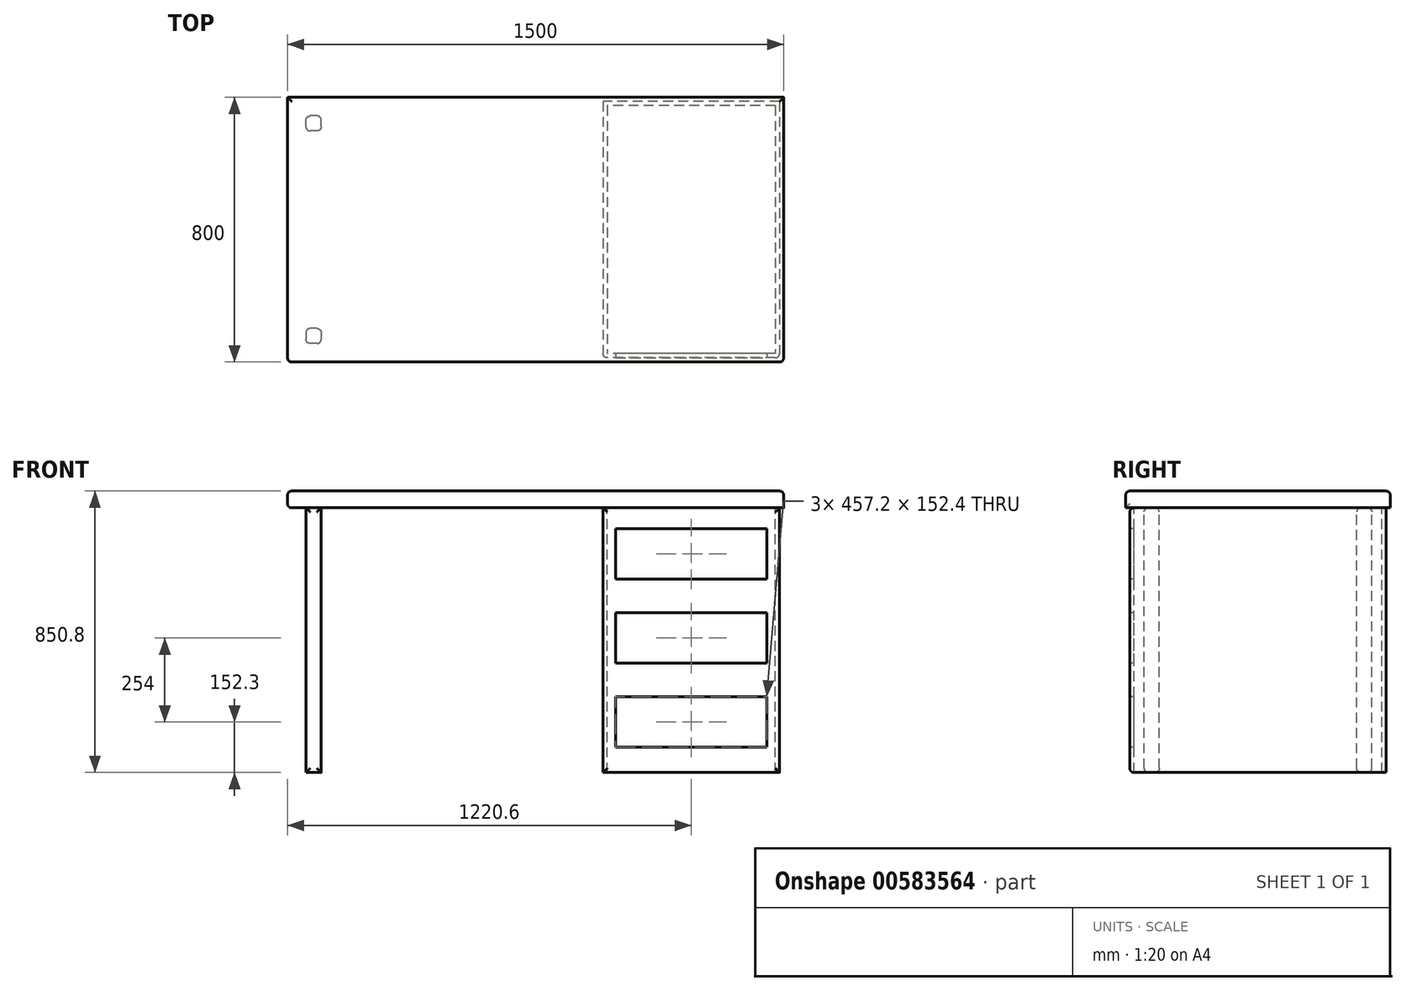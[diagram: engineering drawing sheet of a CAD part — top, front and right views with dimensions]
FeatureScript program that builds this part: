
annotation { "Feature Type Name" : "Feature", "Feature Type Description" : "" }
export const myFeature = defineFeature(function(context is Context, id is Id, definition is map)
    precondition{}
    {
        {
            var Q0;
            Q0=qCreatedBy(makeId("Top.planeOp"),FACE);
            var sketch = newSketch(context, id + "F0", { "sketchPlane" : qUnion([Q0])});
            skLineSegment(sketch, "E0.bottom", {"start": v(-750, 400) * mm, "end": v(750, 400) * mm});
            skLineSegment(sketch, "E0.top", {"start": v(-750, -400) * mm, "end": v(750, -400) * mm});
            skLineSegment(sketch, "E0.left", {"start": v(-750, 400) * mm, "end": v(-750, -400) * mm});
            skLineSegment(sketch, "E0.right", {"start": v(750, 400) * mm, "end": v(750, -400) * mm});
            skPoint(sketch, "E0.middle", {"position": v(0, 0) * mm});
            skSolve(sketch);
        }
        {
            var Q0;
            Q0 = qSketchRegion(id + "F0", true);
            extrude(context, id + "F1", {"entities" : qUnion([Q0]), "depth" : 50.8 * mm, "offsetDistance" : 25.4 * mm});
        }
        {
            var Q0;
            Q0=makeQuery(id+"F1.opExtrude","CAP_FACE",FACE,{"disambiguationData":[OSD([sQuery(id+"F0.wireOp",EDGE,"E0.bottom"),sQuery(id+"F0.wireOp",EDGE,"E0.top"),sQuery(id+"F0.wireOp",EDGE,"E0.left"),sQuery(id+"F0.wireOp",EDGE,"E0.right")])],"isStart":true});
            var sketch = newSketch(context, id + "F2", { "sketchPlane" : qUnion([Q0])});
            skLineSegment(sketch, "E1.bottom", {"start": v(-648.4, 298.4) * mm, "end": v(-694.12, 298.4) * mm});
            skLineSegment(sketch, "E1.top", {"start": v(-648.4, 344.12) * mm, "end": v(-694.12, 344.12) * mm});
            skLineSegment(sketch, "E1.left", {"start": v(-648.4, 298.4) * mm, "end": v(-648.4, 344.12) * mm});
            skLineSegment(sketch, "E1.right", {"start": v(-694.12, 298.4) * mm, "end": v(-694.12, 344.12) * mm});
            skPoint(sketch, "E1.middle", {"position": v(-671.26, 321.26) * mm});
            skLineSegment(sketch, "E2", {"start": v(0, 0) * mm, "end": v(-399.1, 0) * mm, "construction": true});
            skPoint(sketch, "E3.MirrorP", {"position": v(-671.26, -321.26) * mm});
            skLineSegment(sketch, "E4.MirrorCS", {"start": v(-648.4, -298.4) * mm, "end": v(-694.12, -298.4) * mm});
            skLineSegment(sketch, "E5.MirrorCS", {"start": v(-648.4, -344.12) * mm, "end": v(-694.12, -344.12) * mm});
            skLineSegment(sketch, "E6.MirrorCS", {"start": v(-648.4, -298.4) * mm, "end": v(-648.4, -344.12) * mm});
            skLineSegment(sketch, "E7.MirrorCS", {"start": v(-694.12, -298.4) * mm, "end": v(-694.12, -344.12) * mm});
            skSolve(sketch);
        }
        {
            var Q0;
            Q0=makeQuery(id+"F2.imprint","IMPRINT",FACE,{"disambiguationData":[TD([[makeQuery(id+"F2.imprint","IMPRINT",EDGE,{"derivedFrom":sQuery(id+"F2.wireOp",EDGE,"E1.bottom")}),-1.0]])]});
            var Q1;
            Q1=makeQuery(id+"F2.imprint","IMPRINT",FACE,{"disambiguationData":[TD([[makeQuery(id+"F2.imprint","IMPRINT",EDGE,{"derivedFrom":sQuery(id+"F2.wireOp",EDGE,"E4.MirrorCS")}),1.0]])]});
            extrude(context, id + "F3", {"entities" : qUnion([Q0, Q1]), "depth" : 800 * mm, "offsetDistance" : 25.4 * mm});
        }
        {
            var Q0;
            Q0=makeQuery(id+"F1.opExtrude","CAP_FACE",FACE,{"disambiguationData":[OSD([sQuery(id+"F0.wireOp",EDGE,"E0.bottom"),sQuery(id+"F0.wireOp",EDGE,"E0.top"),sQuery(id+"F0.wireOp",EDGE,"E0.left"),sQuery(id+"F0.wireOp",EDGE,"E0.right")])],"isStart":true});
            var sketch = newSketch(context, id + "F4", { "sketchPlane" : qUnion([Q0])});
            skLineSegment(sketch, "E8.bottom", {"start": v(724.6, -374.6) * mm, "end": v(216.6, -374.6) * mm});
            skLineSegment(sketch, "E8.top", {"start": v(724.6, 374.6) * mm, "end": v(216.6, 374.6) * mm});
            skLineSegment(sketch, "E8.left", {"start": v(724.6, -374.6) * mm, "end": v(724.6, 374.6) * mm});
            skLineSegment(sketch, "E8.right", {"start": v(216.6, -374.6) * mm, "end": v(216.6, 374.6) * mm});
            skPoint(sketch, "E8.middle", {"position": v(470.6, 0) * mm});
            skLineSegment(sketch, "E9.0", {"start": v(203.9, -387.3) * mm, "end": v(203.9, 387.3) * mm});
            skLineSegment(sketch, "E9.1", {"start": v(737.3, -387.3) * mm, "end": v(203.9, -387.3) * mm});
            skLineSegment(sketch, "E9.2", {"start": v(737.3, -387.3) * mm, "end": v(737.3, 387.3) * mm});
            skLineSegment(sketch, "E9.3", {"start": v(737.3, 387.3) * mm, "end": v(203.9, 387.3) * mm});
            skSolve(sketch);
        }
        {
            var Q0;
            Q0 = qSketchRegion(id + "F4", true);
            extrude(context, id + "F5", {"entities" : qUnion([Q0]), "depth" : 800 * mm, "offsetDistance" : 25.4 * mm});
        }
        {
            var Q0;
            Q0=makeQuery(id+"F5.opExtrude","SWEPT_FACE",FACE,{"disambiguationData":[OSD([sQuery(id+"F4.wireOp",EDGE,"E9.3")])]});
            var Q1;
            Q1=makeQuery(id+"F1.opExtrude","CAP_FACE",FACE,{"disambiguationData":[OSD([sQuery(id+"F0.wireOp",EDGE,"E0.bottom"),sQuery(id+"F0.wireOp",EDGE,"E0.top"),sQuery(id+"F0.wireOp",EDGE,"E0.left"),sQuery(id+"F0.wireOp",EDGE,"E0.right")])],"isStart":false});
            var Q2;
            Q2=makeQuery(id+"F1.opExtrude","CAP_EDGE",EDGE,{"disambiguationData":[OSD([sQuery(id+"F0.wireOp",EDGE,"E0.left")])],"isStart":true});
            var Q3;
            Q3=makeQuery(id+"F3.opExtrude","SWEPT_FACE",FACE,{"disambiguationData":[OSD([sQuery(id+"F2.wireOp",EDGE,"E1.top")])]});
            var Q4;
            Q4=makeQuery(id+"F3.opExtrude","SWEPT_FACE",FACE,{"disambiguationData":[OSD([sQuery(id+"F2.wireOp",EDGE,"E4.MirrorCS")])]});
            var Q5;
            Q5=makeQuery(id+"F3.opExtrude","SWEPT_FACE",FACE,{"disambiguationData":[OSD([sQuery(id+"F2.wireOp",EDGE,"E5.MirrorCS")])]});
            var Q6;
            Q6=makeQuery(id+"F3.opExtrude","SWEPT_FACE",FACE,{"disambiguationData":[OSD([sQuery(id+"F2.wireOp",EDGE,"E1.bottom")])]});
            var Q7;
            Q7=makeQuery(id+"F1.opExtrude","SWEPT_EDGE",EDGE,{"disambiguationData":[OSD([sQuery(id+"F0.wireOp",EDGE,"E0.top"),sQuery(id+"F0.wireOp",EDGE,"E0.left")])]});
            var Q8;
            Q8=makeQuery(id+"F1.opExtrude","SWEPT_EDGE",EDGE,{"disambiguationData":[OSD([sQuery(id+"F0.wireOp",EDGE,"E0.top"),sQuery(id+"F0.wireOp",EDGE,"E0.right")])]});
            fillet(context, id + "F6", {"entities" : qUnion([Q0, Q1, Q2, Q3, Q4, Q5, Q6, Q7, Q8]), "radius" : 12.7 * mm, "tangentPropagation" : true, "allowEdgeOverflow" : false});
        }
        {
            var Q0;
            Q0=makeQuery(id+"F5.opExtrude","SWEPT_FACE",FACE,{"disambiguationData":[OSD([sQuery(id+"F4.wireOp",EDGE,"E9.3")])]});
            var sketch = newSketch(context, id + "F7", { "sketchPlane" : qUnion([Q0])});
            skLineSegment(sketch, "E10.bottom", {"start": v(242, -63.5) * mm, "end": v(699.2, -63.5) * mm});
            skLineSegment(sketch, "E10.top", {"start": v(242, -215.9) * mm, "end": v(699.2, -215.9) * mm});
            skLineSegment(sketch, "E10.left", {"start": v(242, -63.5) * mm, "end": v(242, -215.9) * mm});
            skLineSegment(sketch, "E10.right", {"start": v(699.2, -63.5) * mm, "end": v(699.2, -215.9) * mm});
            skLineSegment(sketch, "E11.0.1.0", {"start": v(242, -317.5) * mm, "end": v(699.2, -317.5) * mm});
            skLineSegment(sketch, "E11.0.1.1", {"start": v(242, -317.5) * mm, "end": v(242, -469.9) * mm});
            skLineSegment(sketch, "E11.0.1.2", {"start": v(242, -469.9) * mm, "end": v(699.2, -469.9) * mm});
            skLineSegment(sketch, "E11.0.1.3", {"start": v(699.2, -317.5) * mm, "end": v(699.2, -469.9) * mm});
            skLineSegment(sketch, "E11.0.2.0", {"start": v(242, -571.5) * mm, "end": v(699.2, -571.5) * mm});
            skLineSegment(sketch, "E11.0.2.1", {"start": v(242, -571.5) * mm, "end": v(242, -723.9) * mm});
            skLineSegment(sketch, "E11.0.2.2", {"start": v(242, -723.9) * mm, "end": v(699.2, -723.9) * mm});
            skLineSegment(sketch, "E11.0.2.3", {"start": v(699.2, -571.5) * mm, "end": v(699.2, -723.9) * mm});
            skLineSegment(sketch, "E11.direction1", {"start": v(242, -215.9) * mm, "end": v(242, -215.9) * mm});
            skLineSegment(sketch, "E11.direction2", {"start": v(242, -215.9) * mm, "end": v(242, -469.9) * mm, "construction": true});
            skSolve(sketch);
        }
        {
            var Q0;
            Q0=makeQuery(id+"F7.imprint","IMPRINT",FACE,{"disambiguationData":[TD([[makeQuery(id+"F7.imprint","IMPRINT",EDGE,{"derivedFrom":sQuery(id+"F7.wireOp",EDGE,"E10.bottom")}),-1.0]])]});
            var Q1;
            Q1=makeQuery(id+"F7.imprint","IMPRINT",FACE,{"disambiguationData":[TD([[makeQuery(id+"F7.imprint","IMPRINT",EDGE,{"derivedFrom":sQuery(id+"F7.wireOp",EDGE,"E11.0.1.0")}),-1.0]])]});
            var Q2;
            Q2=makeQuery(id+"F7.imprint","IMPRINT",FACE,{"disambiguationData":[TD([[makeQuery(id+"F7.imprint","IMPRINT",EDGE,{"derivedFrom":sQuery(id+"F7.wireOp",EDGE,"E11.0.2.0")}),-1.0]])]});
            extrude(context, id + "F8", {"entities" : qUnion([Q0, Q1, Q2]), "operationType" : NewBodyOperationType.REMOVE, "oppositeDirection" : true, "depth" : 25.4 * mm, "offsetDistance" : 25.4 * mm});
        }
    });
